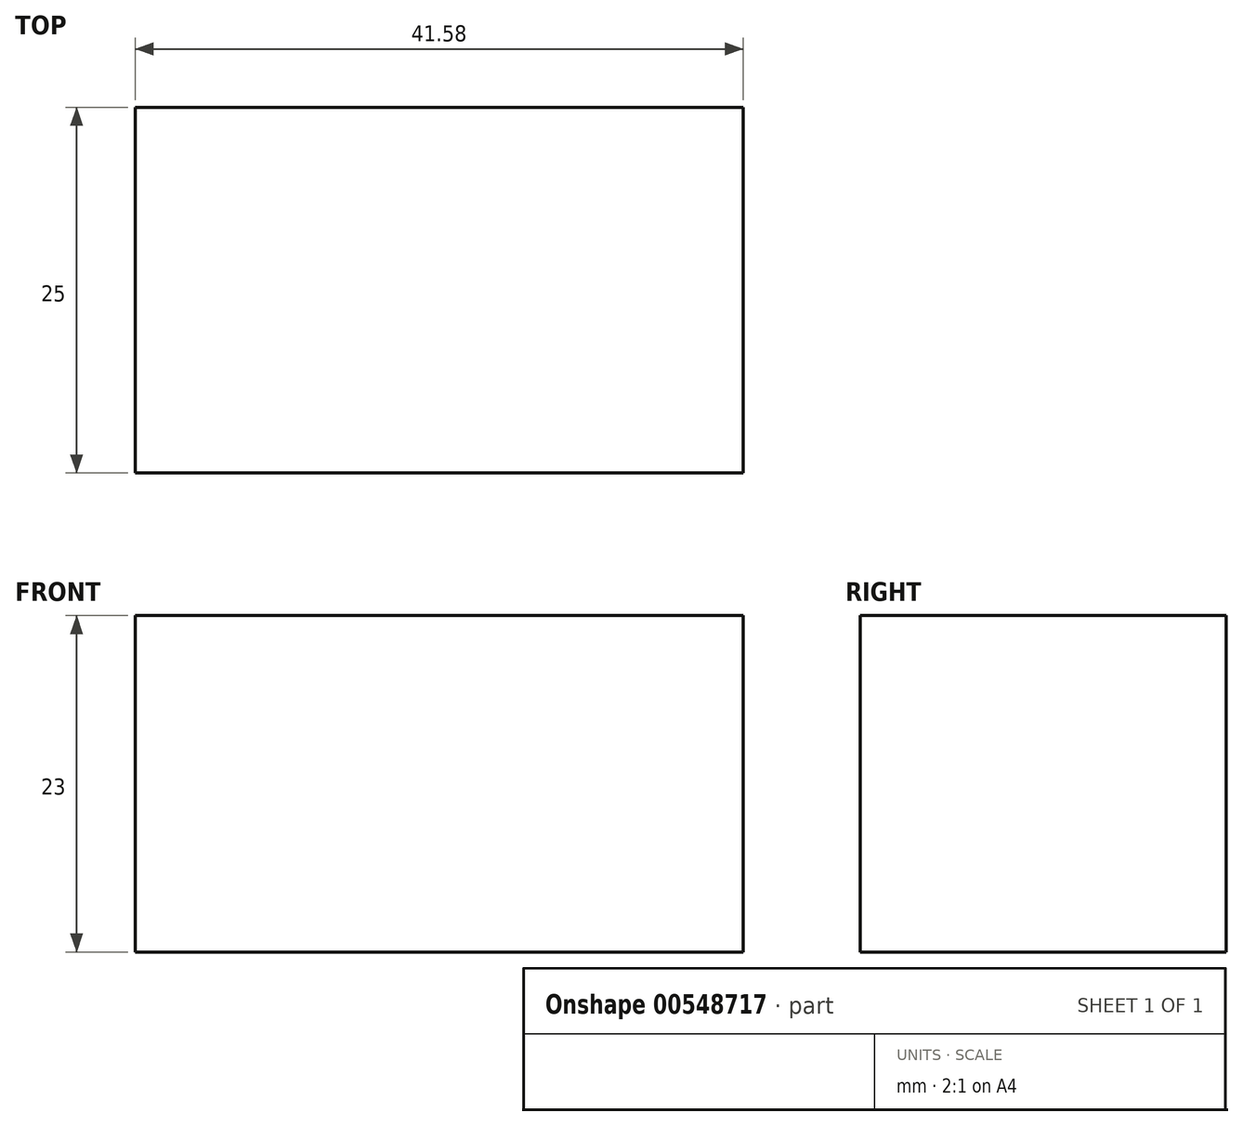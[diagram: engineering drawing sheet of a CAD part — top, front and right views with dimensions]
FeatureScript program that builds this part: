
annotation { "Feature Type Name" : "Feature", "Feature Type Description" : "" }
export const myFeature = defineFeature(function(context is Context, id is Id, definition is map)
    precondition{}
    {
        {
            var Q0;
            Q0=qCreatedBy(makeId("Front.planeOp"),FACE);
            var sketch = newSketch(context, id + "F0", { "sketchPlane" : qUnion([Q0])});
            skLineSegment(sketch, "E0.bottom", {"start": v(0, 0) * mm, "end": v(-41.58, 0) * mm});
            skLineSegment(sketch, "E0.top", {"start": v(0, 23) * mm, "end": v(-41.58, 23) * mm});
            skLineSegment(sketch, "E0.left", {"start": v(0, 0) * mm, "end": v(0, 23) * mm});
            skLineSegment(sketch, "E0.right", {"start": v(-41.58, 0) * mm, "end": v(-41.58, 23) * mm});
            skSolve(sketch);
        }
        {
            var Q0;
            Q0 = qSketchRegion(id + "F0", true);
            extrude(context, id + "F1", {"entities" : qUnion([Q0]), "depth" : 25 * mm, "offsetDistance" : 25 * mm});
        }
    });
